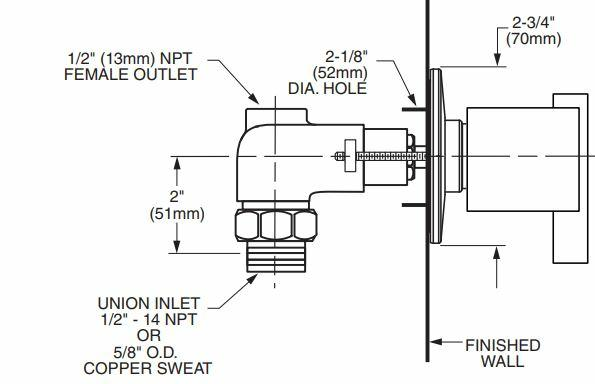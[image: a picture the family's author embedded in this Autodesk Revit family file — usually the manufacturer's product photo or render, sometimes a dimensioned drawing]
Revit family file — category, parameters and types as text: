
# Revit family: Diverter-American_Standard-Boulevard-T431_Series
name_source: partatom
category: Plumbing Fixtures
revit_build: Autodesk Revit 2015 (Build: 20140606_1530(x64)
units: mm (PartAtom-declared; Revit-internal decimal feet)

## types (2) — shared parameters
Assembly Code = D2020300
CW Connection = Yes
Cold Water Connection Diameter = 1/2"
Cold Water Connection Radius = 1/4"
Default Elevation = 48"
Description = Boulevard Diverter Valve Trim Kit
HW Connection = Yes
Height = 3"
Hot Water Connection Diameter = 1"
Hot Water Connection Radius = 1/4"
Installation Type = Wall Mounted
Length = 3 7/8"
Manufacturer = American Standard
Price = Prices may vary. Please consult Manufacturer Representative for most up-to-date price list.
Product Documentation Link = https://americanstandard.ca
Product Page URL = https://americanstandard.ca
Tempered Water Connection Diameter = 1/2"
Tempered Water Connection Radius = 1/4"
URL = https://americanstandard.ca
Width = 2 3/4"

## per-type parameters (varying)
| type | Finish | Material |
| T431.430.002 | Brass-American Standard-002-Chrome | Brass-American Standard-002-Chrome |
| T431.430.295 | Brass-American Standard-295-Brushed Nickel | Brass-American Standard-295-Brushed Nickel |

note: column(s) folded — value = type name in every type: Model

## geometry (parser evidence)
native form markers: Sweep x3
no freeform markers — native parametric forms only
